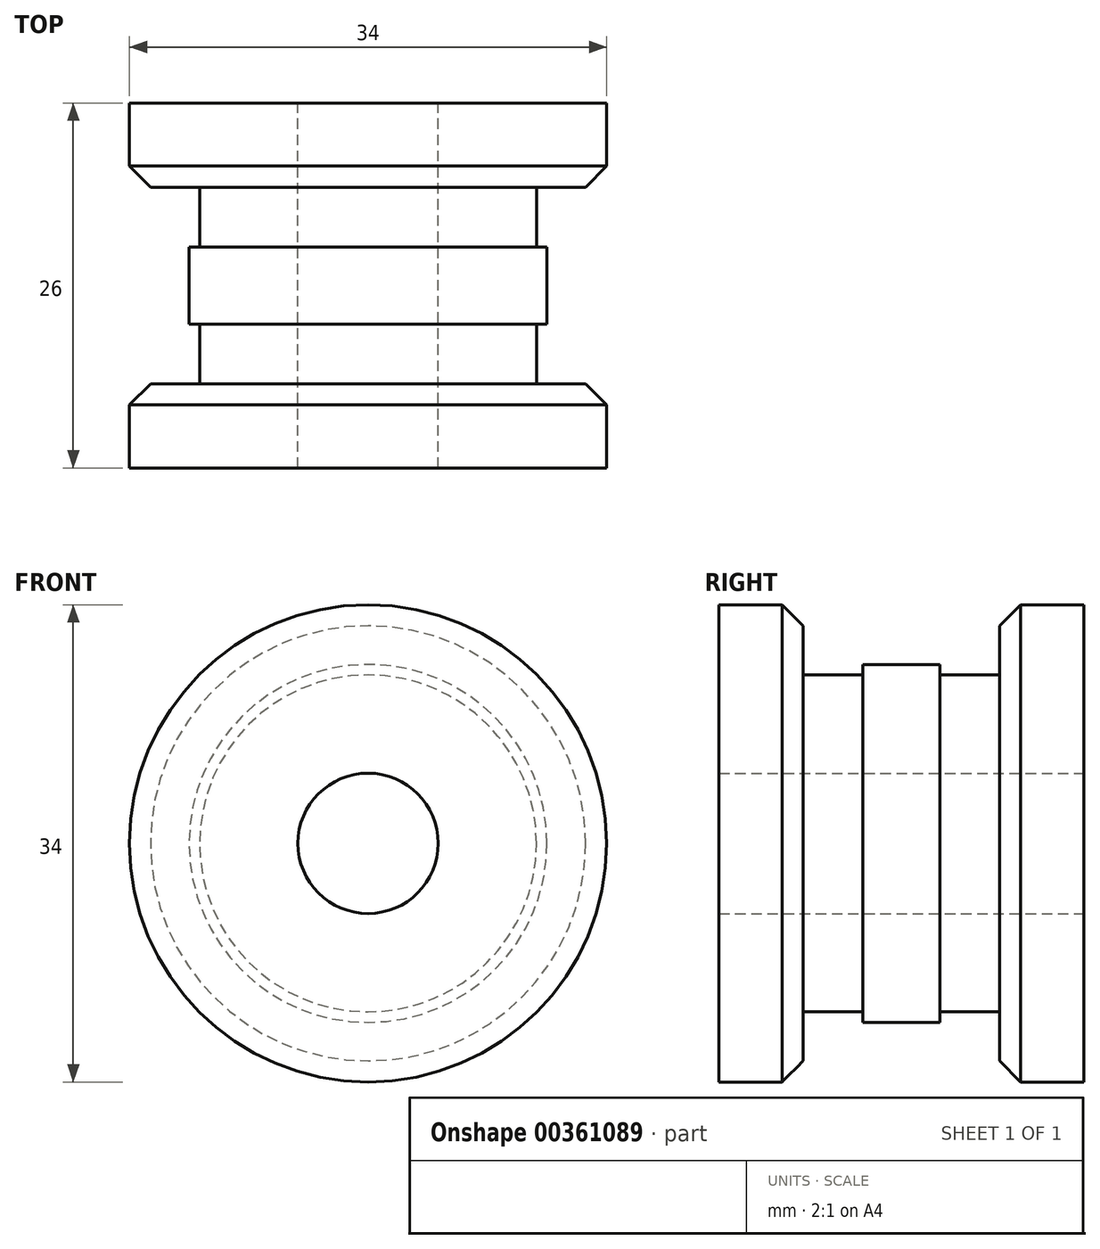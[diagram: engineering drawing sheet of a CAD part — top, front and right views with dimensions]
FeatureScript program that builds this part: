
annotation { "Feature Type Name" : "Feature", "Feature Type Description" : "" }
export const myFeature = defineFeature(function(context is Context, id is Id, definition is map)
    precondition{}
    {
        {
            var Q0;
            Q0=qCreatedBy(makeId("Front.planeOp"),FACE);
            var sketch = newSketch(context, id + "F0", { "sketchPlane" : qUnion([Q0])});
            skCircle(sketch, "E0", {"center": v(-137.71, -19.46) * mm, "radius": 5 * mm});
            skCircle(sketch, "E1", {"center": v(-137.71, -19.46) * mm, "radius": 12 * mm});
            skCircle(sketch, "E2", {"center": v(-137.71, -19.46) * mm, "radius": 12.75 * mm});
            skCircle(sketch, "E3", {"center": v(-137.71, -19.46) * mm, "radius": 17 * mm});
            skSolve(sketch);
        }
        {
            var Q0;
            Q0=makeQuery(id+"F0.imprint","IMPRINT",FACE,{"disambiguationData":[TD([[makeQuery(id+"F0.imprint","IMPRINT",EDGE,{"derivedFrom":sQuery(id+"F0.wireOp",EDGE,"E0")}),-1.0]])]});
            extrude(context, id + "F1", {"entities" : qUnion([Q0]), "endBound" : BoundingType.SYMMETRIC, "depth" : 14 * mm});
        }
        {
            var Q0;
            Q0=makeQuery(id+"F0.imprint","IMPRINT",FACE,{"disambiguationData":[TD([[makeQuery(id+"F0.imprint","IMPRINT",EDGE,{"derivedFrom":sQuery(id+"F0.wireOp",EDGE,"E1")}),-1.0]])]});
            extrude(context, id + "F2", {"entities" : qUnion([Q0]), "operationType" : NewBodyOperationType.ADD, "endBound" : BoundingType.SYMMETRIC, "depth" : 5.5 * mm});
        }
        {
            var Q0;
            Q0=makeQuery(id+"F1.opExtrude","CAP_FACE",FACE,{"disambiguationData":[OSD([sQuery(id+"F0.wireOp",EDGE,"E0"),sQuery(id+"F0.wireOp",EDGE,"E1")])],"isStart":false});
            var sketch = newSketch(context, id + "F3", { "sketchPlane" : qUnion([Q0])});
            skCircle(sketch, "E4", {"center": v(-137.71, -19.46) * mm, "radius": 5 * mm});
            skCircle(sketch, "E5", {"center": v(-137.71, -19.46) * mm, "radius": 17 * mm});
            skSolve(sketch);
        }
        {
            var Q0;
            Q0 = qSketchRegion(id + "F3", true);
            extrude(context, id + "F4", {"entities" : qUnion([Q0]), "operationType" : NewBodyOperationType.ADD, "depth" : 6 * mm});
        }
        {
            var Q0;
            Q0=makeQuery(id+"F4.opExtrude","CAP_EDGE",EDGE,{"disambiguationData":[OSD([sQuery(id+"F3.wireOp",EDGE,"E5")])],"isStart":true});
            chamfer(context, id + "F5", {"entities" : qUnion([Q0]), "width" : 1.5 * mm, "tangentPropagation" : true});
        }
        {
            var Q0;
            Q0=makeQuery(id+"F1.opExtrude","CAP_FACE",FACE,{"disambiguationData":[OSD([sQuery(id+"F0.wireOp",EDGE,"E0"),sQuery(id+"F0.wireOp",EDGE,"E1")])],"isStart":true});
            var sketch = newSketch(context, id + "F6", { "sketchPlane" : qUnion([Q0])});
            skCircle(sketch, "E6", {"center": v(137.71, -19.46) * mm, "radius": 17 * mm});
            skCircle(sketch, "E7", {"center": v(137.71, -19.46) * mm, "radius": 5 * mm});
            skSolve(sketch);
        }
        {
            var Q0;
            Q0=makeQuery(id+"F6.imprint","IMPRINT",FACE,{"disambiguationData":[TD([[makeQuery(id+"F6.imprint","IMPRINT",EDGE,{"derivedFrom":sQuery(id+"F6.wireOp",EDGE,"E7")}),1.0]])]});
            var Q1;
            Q1=makeQuery(id+"F6.imprint","IMPRINT",FACE,{"disambiguationData":[TD([[makeQuery(id+"F6.imprint","IMPRINT",EDGE,{"derivedFrom":sQuery(id+"F6.wireOp",EDGE,"E6")}),1.0]])]});
            extrude(context, id + "F7", {"entities" : qUnion([Q0, Q1]), "operationType" : NewBodyOperationType.ADD, "depth" : 6 * mm});
        }
        {
            var Q0;
            Q0=makeQuery(id+"F7.opExtrude","CAP_EDGE",EDGE,{"disambiguationData":[OSD([sQuery(id+"F6.wireOp",EDGE,"E6")])],"isStart":true});
            chamfer(context, id + "F8", {"entities" : qUnion([Q0]), "width" : 1.5 * mm, "tangentPropagation" : true});
        }
    });
